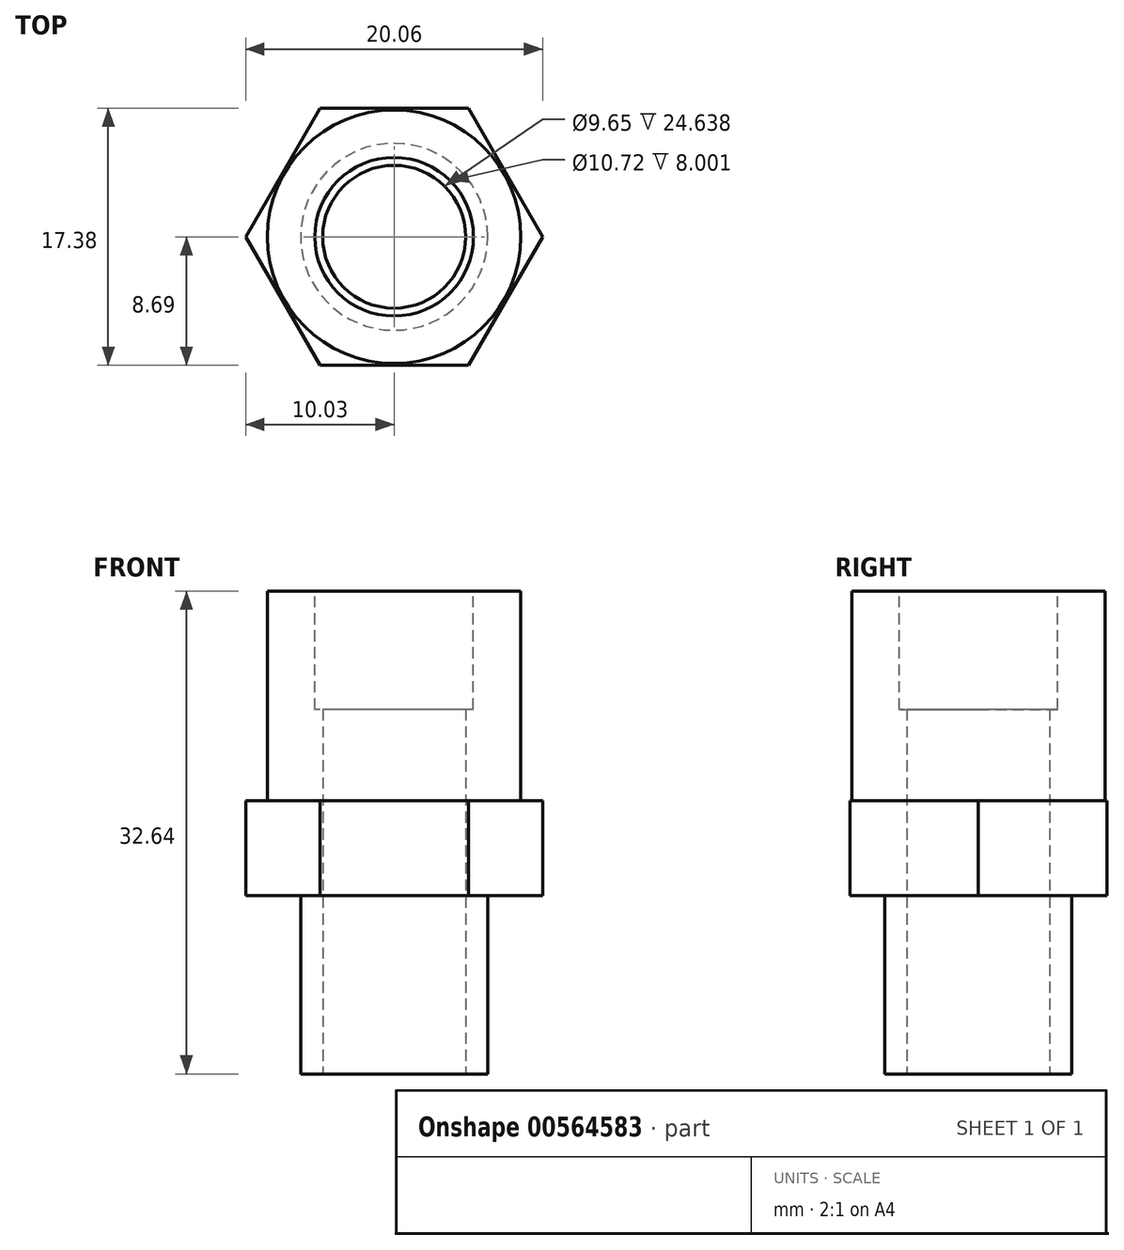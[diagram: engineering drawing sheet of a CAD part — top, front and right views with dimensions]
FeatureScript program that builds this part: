
annotation { "Feature Type Name" : "Feature", "Feature Type Description" : "" }
export const myFeature = defineFeature(function(context is Context, id is Id, definition is map)
    precondition{}
    {
        {
            var Q0;
            Q0=qCreatedBy(makeId("Top.planeOp"),FACE);
            var sketch = newSketch(context, id + "F0", { "sketchPlane" : qUnion([Q0])});
            skCircle(sketch, "E0", {"center": v(0, 0) * mm, "radius": 8.57 * mm});
            skCircle(sketch, "E1", {"center": v(0, 0) * mm, "radius": 4.83 * mm});
            skSolve(sketch);
        }
        {
            var Q0;
            Q0 = qSketchRegion(id + "F0", true);
            extrude(context, id + "F1", {"entities" : qUnion([Q0]), "depth" : 32.64 * mm, "offsetDistance" : 25.4 * mm});
        }
        {
            var Q0;
            Q0=makeQuery(id+"F1.opExtrude","CAP_FACE",FACE,{"disambiguationData":[OSD([sQuery(id+"F0.wireOp",EDGE,"E0"),sQuery(id+"F0.wireOp",EDGE,"E1")])],"isStart":true});
            var sketch = newSketch(context, id + "F2", { "sketchPlane" : qUnion([Q0])});
            skCircle(sketch, "E2", {"center": v(0, 0) * mm, "radius": 6.32 * mm});
            skCircle(sketch, "E3", {"center": v(0, 0) * mm, "radius": 16.12 * mm});
            skSolve(sketch);
        }
        {
            var Q0;
            Q0 = qSketchRegion(id + "F2", true);
            extrude(context, id + "F3", {"entities" : qUnion([Q0]), "operationType" : NewBodyOperationType.REMOVE, "oppositeDirection" : true, "depth" : 12.05 * mm, "offsetDistance" : 25.4 * mm});
        }
        {
            var Q0;
            Q0=makeQuery(id+"F3.boolean.opBoolean","COPY",FACE,{"derivedFrom":makeQuery(id+"F3.opExtrude","CAP_FACE",FACE,{"disambiguationData":[OSD([sQuery(id+"F2.wireOp",EDGE,"E2"),sQuery(id+"F2.wireOp",EDGE,"E3")])],"isStart":false})});
            var sketch = newSketch(context, id + "F4", { "sketchPlane" : qUnion([Q0])});
            skCircle(sketch, "E4.cCircle", {"center": v(0, 0) * mm, "radius": 8.69 * mm, "construction": true});
            skLineSegment(sketch, "E4.0", {"start": v(-5.02, 8.69) * mm, "end": v(5.02, 8.69) * mm});
            skLineSegment(sketch, "E4.1", {"start": v(5.02, 8.69) * mm, "end": v(10.03, 0) * mm});
            skLineSegment(sketch, "E4.2", {"start": v(10.03, 0) * mm, "end": v(5.02, -8.69) * mm});
            skLineSegment(sketch, "E4.3", {"start": v(5.02, -8.69) * mm, "end": v(-5.02, -8.69) * mm});
            skLineSegment(sketch, "E4.4", {"start": v(-5.02, -8.69) * mm, "end": v(-10.03, 0) * mm});
            skLineSegment(sketch, "E4.5", {"start": v(-10.03, 0) * mm, "end": v(-5.02, 8.69) * mm});
            skPoint(sketch, "E4.0.midPoint", {"position": v(0, 8.69) * mm});
            skCircle(sketch, "E5", {"center": v(0, 0) * mm, "radius": 4.83 * mm});
            skSolve(sketch);
        }
        {
            var Q0;
            Q0 = qSketchRegion(id + "F4", true);
            extrude(context, id + "F5", {"entities" : qUnion([Q0]), "operationType" : NewBodyOperationType.ADD, "oppositeDirection" : true, "depth" : 6.4 * mm, "offsetDistance" : 25.4 * mm});
        }
        {
            var Q0;
            Q0=makeQuery(id+"F1.opExtrude","CAP_FACE",FACE,{"disambiguationData":[OSD([sQuery(id+"F0.wireOp",EDGE,"E0"),sQuery(id+"F0.wireOp",EDGE,"E1")])],"isStart":false});
            var sketch = newSketch(context, id + "F6", { "sketchPlane" : qUnion([Q0])});
            skCircle(sketch, "E6", {"center": v(0, 0) * mm, "radius": 5.36 * mm});
            skSolve(sketch);
        }
        {
            var Q0;
            Q0 = qSketchRegion(id + "F6", true);
            extrude(context, id + "F7", {"entities" : qUnion([Q0]), "operationType" : NewBodyOperationType.REMOVE, "oppositeDirection" : true, "depth" : 8 * mm, "offsetDistance" : 25.4 * mm});
        }
    });
